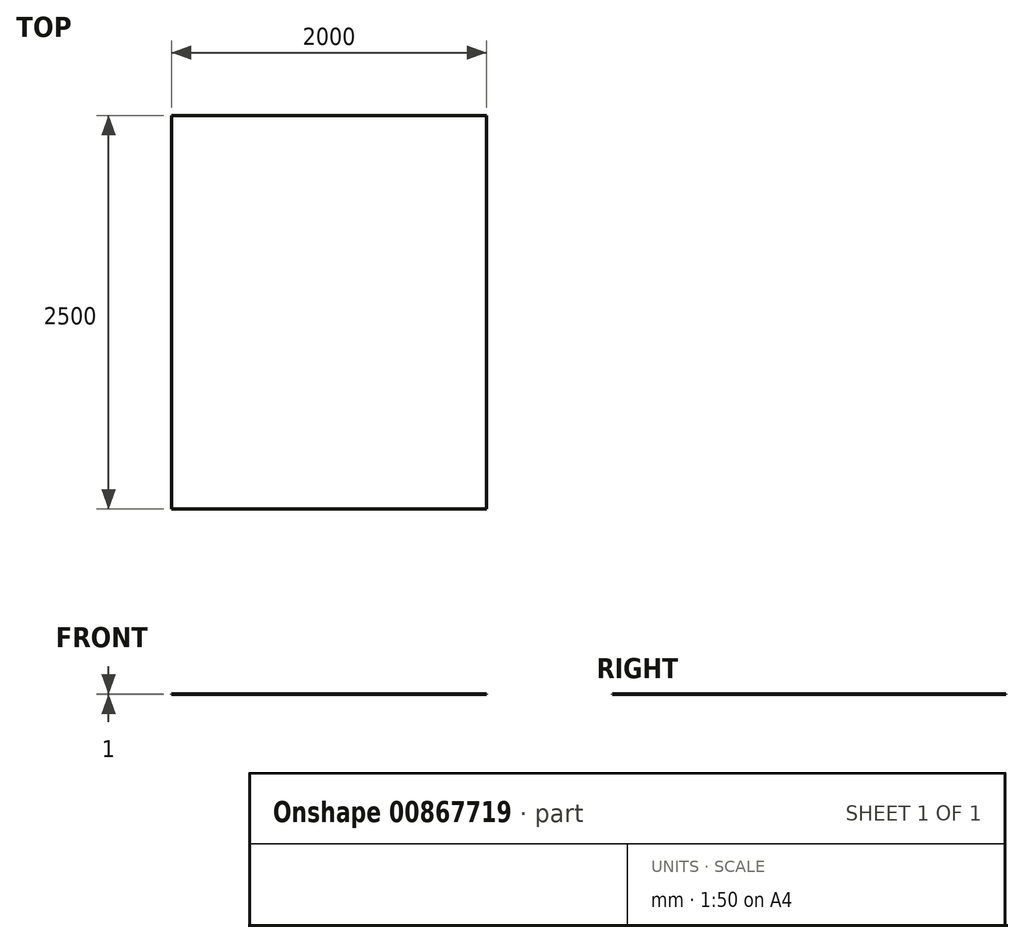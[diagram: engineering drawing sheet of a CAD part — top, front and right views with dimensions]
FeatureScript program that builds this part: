
annotation { "Feature Type Name" : "Feature", "Feature Type Description" : "" }
export const myFeature = defineFeature(function(context is Context, id is Id, definition is map)
    precondition{}
    {
        {
            var Q0;
            Q0=qCreatedBy(makeId("Top.planeOp"),FACE);
            var sketch = newSketch(context, id + "F0", { "sketchPlane" : qUnion([Q0])});
            skLineSegment(sketch, "E0.bottom", {"start": v(-1989.69, 2466.43) * mm, "end": v(10.31, 2466.43) * mm});
            skLineSegment(sketch, "E0.top", {"start": v(-1989.69, -33.57) * mm, "end": v(10.31, -33.57) * mm});
            skLineSegment(sketch, "E0.left", {"start": v(-1989.69, 2466.43) * mm, "end": v(-1989.69, -33.57) * mm});
            skLineSegment(sketch, "E0.right", {"start": v(10.31, 2466.43) * mm, "end": v(10.31, -33.57) * mm});
            skSolve(sketch);
        }
        {
            var Q0;
            Q0=makeQuery(id+"F0.imprint","IMPRINT",FACE,{"disambiguationData":[TD([[makeQuery(id+"F0.imprint","IMPRINT",EDGE,{"derivedFrom":sQuery(id+"F0.wireOp",EDGE,"E0.bottom")}),-1.0]])]});
            extrude(context, id + "F1", {"entities" : qUnion([Q0]), "depth" : 1 * mm, "offsetDistance" : 25 * mm});
        }
    });
